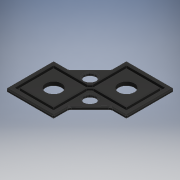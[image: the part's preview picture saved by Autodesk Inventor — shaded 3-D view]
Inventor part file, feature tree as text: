
AUTODESK INVENTOR PART (.ipt)
format: ipt  version: 2018 (Build 220112000, 112)  size: 867,840 bytes
history: native  units: mm
features: other x2, extrude x1, sketch x1
ambient origin geometry x8: Origin, YZ Plane, XZ Plane, XY Plane, X Axis, Y Axis, Z Axis, Center Point
bodies: Solid1 (feature_tree)
feature tree (4):
  other  "27mm_Parasitic_Element"
  other  "MeshFeature1"
  extrude  "Extrusion1"  Depth=2.62mm
  sketch  "Sketch1"  dims[d0=11.0mm d1=11.0mm d2=22.0mm d3=22.0mm d4=2.62mm d5=0.0mm]
